# Revit family: Toilet_Paper_Holder-Reserve-Grohe-Allure-40956_Series
name_source: partatom
category: Specialty Equipment
units: mm (PartAtom-declared; Revit-internal decimal feet)

## family parameters
Cut with Voids When Loaded = No
Host = Face
OmniClass Number = 23.40.20.21
OmniClass Title = Toilet and Bath Specialties
Part Type = Normal
Room Calculation Point = No
Round Connector Dimension = Use Diameter
Shared = Yes

## types (4) — shared parameters
Assembly Code = C1030200
Default Elevation = 40"
Description = Allure Reserve Toilet Paper Holder
Height = 5 7/8"
Installation Type = Councealed Mounting
Length = 5 13/16"
Manufacturer = Grohe
Price = Prices may vary. Please consult Manufacturer Representative for most up-to-date price list.
Product Documentation Link = https://americanstandard.box.com
Product Page URL = https://www.grohe.us
URL = https://www.grohe.us
Width = 2 3/16"

## per-type parameters (varying)
| type | Finish | Material |
| 40956001 | Metal-Grohe-001-StarLight Chrome | Metal-Grohe-001-StarLight Chrome |
| 40956EN1 | Metal-Grohe-EN1-Brushed Nickel Infinity Finish | Metal-Grohe-EN1-Brushed Nickel Infinity Finish |
| 40956GN1 | Metal-Grohe-GN1-Brushed Cool Sunrise | Metal-Grohe-GN1-Brushed Cool Sunrise |
| 409562431 | Metal-Grohe-2431-Matte Black | Metal-Grohe-2431-Matte Black |

note: column(s) folded — value = type name in every type: Model

## geometry (parser evidence)
native form markers: Sweep x5
no freeform markers — native parametric forms only
